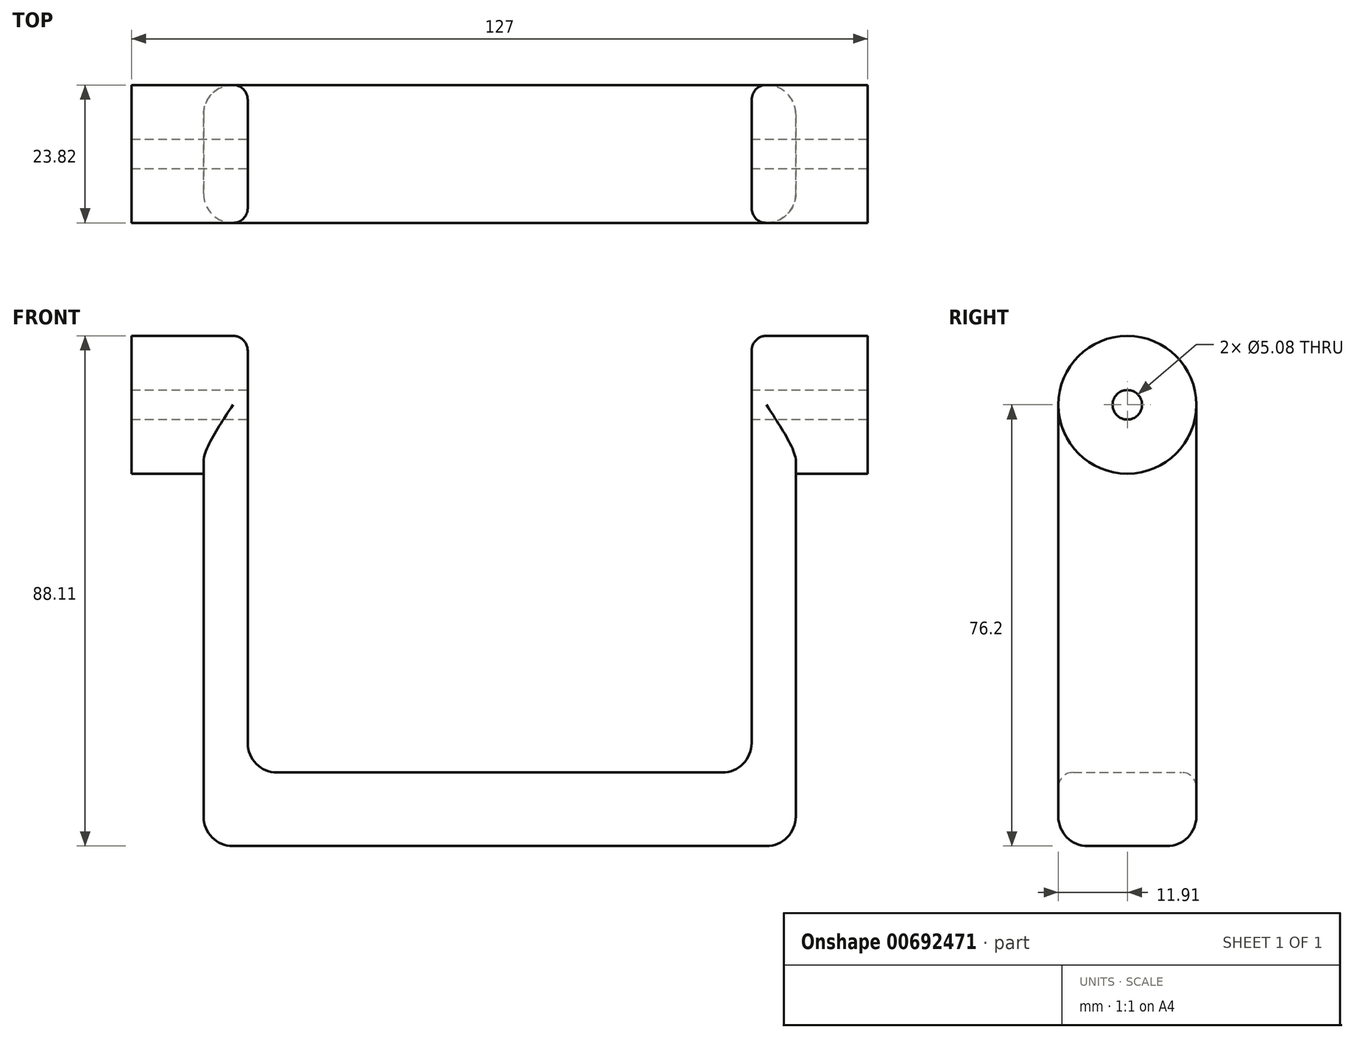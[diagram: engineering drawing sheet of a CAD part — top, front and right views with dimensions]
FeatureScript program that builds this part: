
annotation { "Feature Type Name" : "Feature", "Feature Type Description" : "" }
export const myFeature = defineFeature(function(context is Context, id is Id, definition is map)
    precondition{}
    {
        {
            var Q0;
            Q0=qCreatedBy(makeId("Top.planeOp"),FACE);
            var sketch = newSketch(context, id + "F0", { "sketchPlane" : qUnion([Q0])});
            skLineSegment(sketch, "E0.bottom", {"start": v(-51.1, 11.9) * mm, "end": v(51.1, 11.9) * mm});
            skLineSegment(sketch, "E0.top", {"start": v(-51.1, -11.9) * mm, "end": v(51.1, -11.9) * mm});
            skLineSegment(sketch, "E0.left", {"start": v(-51.1, 11.9) * mm, "end": v(-51.1, -11.9) * mm});
            skLineSegment(sketch, "E0.right", {"start": v(51.1, 11.9) * mm, "end": v(51.1, -11.9) * mm});
            skSolve(sketch);
        }
        {
            var Q0;
            Q0 = qSketchRegion(id + "F0", true);
            extrude(context, id + "F1", {"entities" : qUnion([Q0]), "endBound" : BoundingType.SYMMETRIC, "depth" : 76.2 * mm, "offsetDistance" : 25.4 * mm});
        }
        {
            var Q0;
            Q0=qCreatedBy(makeId("Right.planeOp"),FACE);
            var sketch = newSketch(context, id + "F2", { "sketchPlane" : qUnion([Q0])});
            skCircle(sketch, "E1", {"center": v(0, 38.1) * mm, "radius": 11.9 * mm});
            skSolve(sketch);
        }
        {
            var Q0;
            Q0 = qSketchRegion(id + "F2", true);
            extrude(context, id + "F3", {"entities" : qUnion([Q0]), "operationType" : NewBodyOperationType.ADD, "endBound" : BoundingType.SYMMETRIC, "depth" : 127 * mm, "offsetDistance" : 25.4 * mm});
        }
        {
            var Q0;
            Q0=qCreatedBy(makeId("Front.planeOp"),FACE);
            var sketch = newSketch(context, id + "F4", { "sketchPlane" : qUnion([Q0])});
            skLineSegment(sketch, "E2.bottom", {"start": v(-43.47, 62.83) * mm, "end": v(43.47, 62.83) * mm});
            skLineSegment(sketch, "E2.top", {"start": v(-43.47, -25.4) * mm, "end": v(43.47, -25.4) * mm});
            skLineSegment(sketch, "E2.left", {"start": v(-43.47, 62.83) * mm, "end": v(-43.47, -25.4) * mm});
            skLineSegment(sketch, "E2.right", {"start": v(43.47, 62.83) * mm, "end": v(43.47, -25.4) * mm});
            skSolve(sketch);
        }
        {
            var Q0;
            Q0 = qSketchRegion(id + "F4", true);
            extrude(context, id + "F5", {"entities" : qUnion([Q0]), "operationType" : NewBodyOperationType.REMOVE, "endBound" : BoundingType.SYMMETRIC, "depth" : 50.8 * mm, "offsetDistance" : 25.4 * mm});
        }
        {
            var Q0;
            Q0=qCreatedBy(makeId("Right.planeOp"),FACE);
            var sketch = newSketch(context, id + "F6", { "sketchPlane" : qUnion([Q0])});
            skCircle(sketch, "E3", {"center": v(0, 38.1) * mm, "radius": 2.54 * mm});
            skSolve(sketch);
        }
        {
            var Q0;
            Q0 = qSketchRegion(id + "F6", true);
            extrude(context, id + "F7", {"entities" : qUnion([Q0]), "operationType" : NewBodyOperationType.REMOVE, "endBound" : BoundingType.SYMMETRIC, "oppositeDirection" : true, "depth" : 127 * mm, "offsetDistance" : 25.4 * mm});
        }
        {
            var Q0;
            Q0=makeQuery(id+"F1.opExtrude","SWEPT_EDGE",EDGE,{"disambiguationData":[OSD([sQuery(id+"F0.wireOp",EDGE,"E0.top"),sQuery(id+"F0.wireOp",EDGE,"E0.right")])]});
            var Q1;
            Q1=makeQuery(id+"F1.opExtrude","CAP_EDGE",EDGE,{"disambiguationData":[OSD([sQuery(id+"F0.wireOp",EDGE,"E0.top")])],"isStart":true});
            var Q2;
            Q2=makeQuery(id+"F1.opExtrude","SWEPT_EDGE",EDGE,{"disambiguationData":[OSD([sQuery(id+"F0.wireOp",EDGE,"E0.top"),sQuery(id+"F0.wireOp",EDGE,"E0.left")])]});
            fillet(context, id + "F8", {"entities" : qUnion([Q0, Q1, Q2]), "radius" : 5.08 * mm, "tangentPropagation" : true, "allowEdgeOverflow" : false});
        }
        {
            var Q0;
            Q0=makeQuery(id+"F1.opExtrude","SWEPT_EDGE",EDGE,{"disambiguationData":[OSD([sQuery(id+"F0.wireOp",EDGE,"E0.bottom"),sQuery(id+"F0.wireOp",EDGE,"E0.left")])]});
            var Q1;
            Q1=makeQuery(id+"F1.opExtrude","CAP_EDGE",EDGE,{"disambiguationData":[OSD([sQuery(id+"F0.wireOp",EDGE,"E0.bottom")])],"isStart":true});
            var Q2;
            Q2=makeQuery(id+"F1.opExtrude","SWEPT_EDGE",EDGE,{"disambiguationData":[OSD([sQuery(id+"F0.wireOp",EDGE,"E0.bottom"),sQuery(id+"F0.wireOp",EDGE,"E0.right")])]});
            fillet(context, id + "F9", {"entities" : qUnion([Q0, Q1, Q2]), "radius" : 5.08 * mm, "tangentPropagation" : true, "allowEdgeOverflow" : false});
        }
        {
            var Q0;
            Q0=makeQuery(id+"F1.opExtrude","CAP_EDGE",EDGE,{"disambiguationData":[OSD([sQuery(id+"F0.wireOp",EDGE,"E0.left")])],"isStart":true});
            var Q1;
            Q1=makeQuery(id+"F1.opExtrude","CAP_EDGE",EDGE,{"disambiguationData":[OSD([sQuery(id+"F0.wireOp",EDGE,"E0.right")])],"isStart":true});
            fillet(context, id + "F10", {"entities" : qUnion([Q0, Q1]), "radius" : 5.08 * mm, "tangentPropagation" : true, "allowEdgeOverflow" : false});
        }
        {
            var Q0;
            Q0=makeQuery(id+"F5.boolean.opBoolean","COPY",EDGE,{"derivedFrom":makeQuery(id+"F5.opExtrude","SWEPT_EDGE",EDGE,{"disambiguationData":[OSD([sQuery(id+"F4.wireOp",EDGE,"E2.top"),sQuery(id+"F4.wireOp",EDGE,"E2.left")])]})});
            var Q1;
            Q1=makeQuery(id+"F5.boolean.opBoolean","COPY",EDGE,{"derivedFrom":makeQuery(id+"F5.opExtrude","SWEPT_EDGE",EDGE,{"disambiguationData":[OSD([sQuery(id+"F4.wireOp",EDGE,"E2.top"),sQuery(id+"F4.wireOp",EDGE,"E2.right")])]})});
            fillet(context, id + "F11", {"entities" : qUnion([Q0, Q1]), "radius" : 5.08 * mm, "tangentPropagation" : true, "allowEdgeOverflow" : false});
        }
        {
            var Q0;
            Q0=makeQuery(id+"F5.boolean.opBoolean","INTERSECT",EDGE,{"derivedFrom":[makeQuery(id+"F1.opExtrude","SWEPT_FACE",FACE,{"disambiguationData":[OSD([sQuery(id+"F0.wireOp",EDGE,"E0.top")])]}),makeQuery(id+"F5.opExtrude","SWEPT_FACE",FACE,{"disambiguationData":[OSD([sQuery(id+"F4.wireOp",EDGE,"E2.top")])]})]});
            var Q1;
            Q1=makeQuery(id+"F5.boolean.opBoolean","INTERSECT",EDGE,{"derivedFrom":[makeQuery(id+"F1.opExtrude","SWEPT_FACE",FACE,{"disambiguationData":[OSD([sQuery(id+"F0.wireOp",EDGE,"E0.top")])]}),makeQuery(id+"F5.opExtrude","SWEPT_FACE",FACE,{"disambiguationData":[OSD([sQuery(id+"F4.wireOp",EDGE,"E2.left")])]})]});
            var Q2;
            Q2=makeQuery(id+"F11.opFillet","BLEND_EDGE",EDGE,{"blendedFrom":[makeQuery(id+"F5.boolean.opBoolean","COPY",EDGE,{"derivedFrom":makeQuery(id+"F5.opExtrude","SWEPT_EDGE",EDGE,{"disambiguationData":[OSD([sQuery(id+"F4.wireOp",EDGE,"E2.top"),sQuery(id+"F4.wireOp",EDGE,"E2.left")])]})}),makeQuery(id+"F1.opExtrude","SWEPT_FACE",FACE,{"disambiguationData":[OSD([sQuery(id+"F0.wireOp",EDGE,"E0.top")])]})],"blendedInto":[makeQuery(id+"F1.opExtrude","SWEPT_FACE",FACE,{"disambiguationData":[OSD([sQuery(id+"F0.wireOp",EDGE,"E0.top")])]})]});
            var Q3;
            Q3=makeQuery(id+"F11.opFillet","BLEND_EDGE",EDGE,{"blendedFrom":[makeQuery(id+"F5.boolean.opBoolean","COPY",EDGE,{"derivedFrom":makeQuery(id+"F5.opExtrude","SWEPT_EDGE",EDGE,{"disambiguationData":[OSD([sQuery(id+"F4.wireOp",EDGE,"E2.top"),sQuery(id+"F4.wireOp",EDGE,"E2.right")])]})}),makeQuery(id+"F1.opExtrude","SWEPT_FACE",FACE,{"disambiguationData":[OSD([sQuery(id+"F0.wireOp",EDGE,"E0.top")])]})],"blendedInto":[makeQuery(id+"F1.opExtrude","SWEPT_FACE",FACE,{"disambiguationData":[OSD([sQuery(id+"F0.wireOp",EDGE,"E0.top")])]})]});
            var Q4;
            Q4=makeQuery(id+"F5.boolean.opBoolean","INTERSECT",EDGE,{"derivedFrom":[makeQuery(id+"F1.opExtrude","SWEPT_FACE",FACE,{"disambiguationData":[OSD([sQuery(id+"F0.wireOp",EDGE,"E0.top")])]}),makeQuery(id+"F5.opExtrude","SWEPT_FACE",FACE,{"disambiguationData":[OSD([sQuery(id+"F4.wireOp",EDGE,"E2.right")])]})]});
            fillet(context, id + "F12", {"entities" : qUnion([Q0, Q1, Q2, Q3, Q4]), "radius" : 2.54 * mm, "tangentPropagation" : true, "allowEdgeOverflow" : false});
        }
    });
